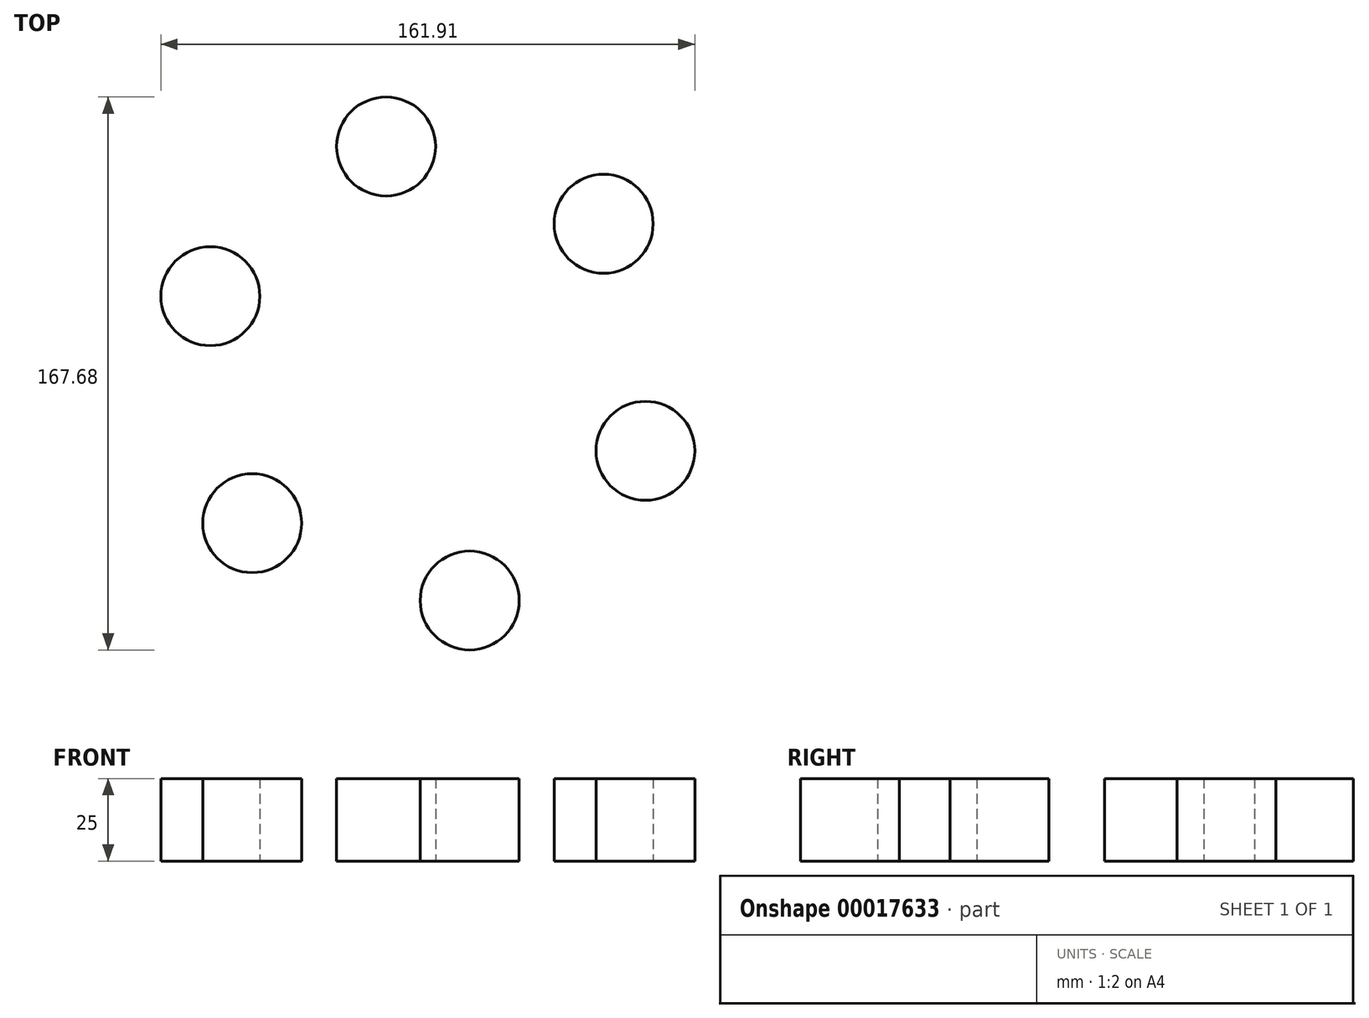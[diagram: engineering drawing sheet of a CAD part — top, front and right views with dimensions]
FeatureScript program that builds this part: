
annotation { "Feature Type Name" : "Feature", "Feature Type Description" : "" }
export const myFeature = defineFeature(function(context is Context, id is Id, definition is map)
    precondition{}
    {
        {
            var Q0;
            Q0=qCreatedBy(makeId("Top.planeOp"),FACE);
            var sketch = newSketch(context, id + "F0", { "sketchPlane" : qUnion([Q0])});
            skCircle(sketch, "E0", {"center": v(-66.21, 24.84) * mm, "radius": 15 * mm});
            skCircle(sketch, "E1.1.0", {"center": v(-53.54, -44) * mm, "radius": 15 * mm});
            skCircle(sketch, "E1.2.0", {"center": v(12.42, -67.45) * mm, "radius": 15 * mm});
            skCircle(sketch, "E1.3.0", {"center": v(65.7, -22.05) * mm, "radius": 15 * mm});
            skCircle(sketch, "E1.4.0", {"center": v(53.03, 46.79) * mm, "radius": 15 * mm});
            skCircle(sketch, "E1.5.0", {"center": v(-12.93, 70.23) * mm, "radius": 15 * mm});
            skPoint(sketch, "E1.center", {"position": v(-0.26, 1.4) * mm});
            skLineSegment(sketch, "E1.anchor1", {"start": v(-0.26, 1.4) * mm, "end": v(-66.21, 24.84) * mm, "construction": true});
            skLineSegment(sketch, "E1.anchor2", {"start": v(-0.26, 1.4) * mm, "end": v(-12.93, 70.23) * mm, "construction": true});
            skSolve(sketch);
        }
        {
            var Q0;
            Q0=makeQuery(id+"F0.imprint","IMPRINT",FACE,{"disambiguationData":[TD([[makeQuery(id+"F0.imprint","IMPRINT",EDGE,{"derivedFrom":sQuery(id+"F0.wireOp",EDGE,"E0")}),1.0]])]});
            var Q1;
            Q1=makeQuery(id+"F0.imprint","IMPRINT",FACE,{"disambiguationData":[TD([[makeQuery(id+"F0.imprint","IMPRINT",EDGE,{"derivedFrom":sQuery(id+"F0.wireOp",EDGE,"E1.5.0")}),1.0]])]});
            var Q2;
            Q2=makeQuery(id+"F0.imprint","IMPRINT",FACE,{"disambiguationData":[TD([[makeQuery(id+"F0.imprint","IMPRINT",EDGE,{"derivedFrom":sQuery(id+"F0.wireOp",EDGE,"E1.4.0")}),1.0]])]});
            var Q3;
            Q3=makeQuery(id+"F0.imprint","IMPRINT",FACE,{"disambiguationData":[TD([[makeQuery(id+"F0.imprint","IMPRINT",EDGE,{"derivedFrom":sQuery(id+"F0.wireOp",EDGE,"E1.3.0")}),1.0]])]});
            var Q4;
            Q4=makeQuery(id+"F0.imprint","IMPRINT",FACE,{"disambiguationData":[TD([[makeQuery(id+"F0.imprint","IMPRINT",EDGE,{"derivedFrom":sQuery(id+"F0.wireOp",EDGE,"E1.2.0")}),1.0]])]});
            var Q5;
            Q5=makeQuery(id+"F0.imprint","IMPRINT",FACE,{"disambiguationData":[TD([[makeQuery(id+"F0.imprint","IMPRINT",EDGE,{"derivedFrom":sQuery(id+"F0.wireOp",EDGE,"E1.1.0")}),1.0]])]});
            extrude(context, id + "F1", {"entities" : qUnion([Q0, Q1, Q2, Q3, Q4, Q5]), "depth" : 25 * mm});
        }
    });
